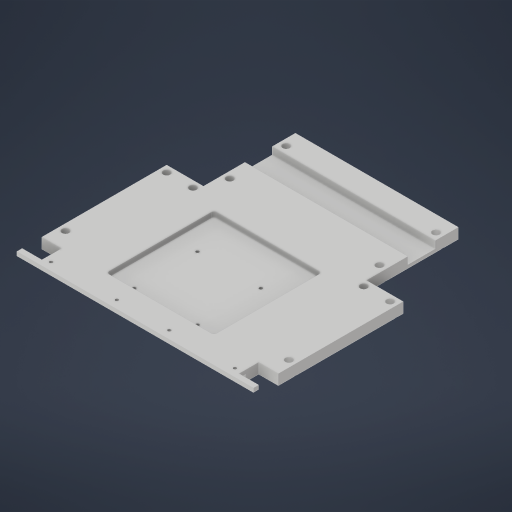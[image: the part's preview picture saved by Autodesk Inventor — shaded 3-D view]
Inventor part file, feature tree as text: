
AUTODESK INVENTOR PART (.ipt)
format: ipt  version: 2023 (Build 270158000, 158)  size: 371,200 bytes
history: native  units: in
note: dims shown in document units (in); Inventor stores cm internally (conversion verified against a paired STEP export)
features: sketch x9, extrude x5, hole x3, fillet x1
ambient origin geometry x8: Origin, YZ Plane, XZ Plane, XY Plane, X Axis, Y Axis, Z Axis, Center Point
bodies: Solid1 (feature_tree)
feature tree (18):
  extrude  "Extrusion1"  Depth=7.0866in
  extrude  "Extrusion2"  Depth=0.1969in TaperAngle=0.0deg
  hole  "Hole1"  [1 undecoded]
  extrude  "Extrusion5"  Depth=0.5906in
  extrude  "Extrusion6"  Depth=0.1181in
  hole  "Hole4"  [1 undecoded]
  hole  "Hole5"  [1 undecoded]
  fillet  "Fillet2"  Radius=3.7402in
  sketch  "Sketch13"  dims[d33=0.097in d34=0.315in d35=0.375in d36=0.25in d37=0.5635in d38=1.0in d39=0.8108in d41=3.7402in]
  extrude  "Extrusion7"  Depth=2.7559in
  sketch  "Sketch1"  dims[d5=0.315in d6=0.0in d7=7.0866in]
  sketch  "Sketch2"  dims[d8=0.3583in d9=0.1969in d10=0.0in]
  sketch  "Sketch6"  dims[d11=0.1575in d12=0.5906in]
  sketch  "Sketch7"  dims[d13=0.5906in d14=0.5906in]
  sketch  "Sketch8"  dims[d15=0.5906in d28=0.1181in]
  sketch  "Sketch11"  dims[d29=0.1969in d30=1.9685in]
  sketch  "Sketch12"  dims[d31=1.5748in d32=1.9685in]
  sketch  "Sketch14"  dims[d42=1.1024in d43=2.7559in d44=2.7559in d45=1.1024in d46=1.1024in d47=0.5906in d48=0.9843in d49=4.8819in d50=0.0in d54=0.1575in d55=0.0in d88=0.1969in d89=0.1969in d92=0.1969in d98=0.2126in d99=0.3937in d100=0.409in d101=0.0591in d102=90.0deg d103=0.3937in d104=0.0in d105=0.1969in d106=0.5118in d107=0.7874in d108=0.7874in d114=1.8898in d115=0.7874in d116=3.2283in d117=3.2283in d119=0.6654in d120=0.1732in d121=1.8976in d122=1.8976in d123=0.097in d124=0.3937in d125=0.375in d126=0.25in d127=0.5635in d128=0.346in d129=0.0in d130=0.0787in d131=0.1969in d132=0.4724in d133=0.1969in d134=0.4724in d136=0.1969in d137=0.5906in d138=1.5354in d139=0.7913in d140=0.8189in d141=0.2165in d142=0.0in d143=0.375in d144=0.5635in d145=0.75in d146=0.8108in d147=0.0625in d148=0.75in d149=0.375in]
note: 3 required parameter values undecoded (feature->parameter linkage not recoverable at this tier; creation-order binding heuristic only, values carry confidence <= 0.55)
